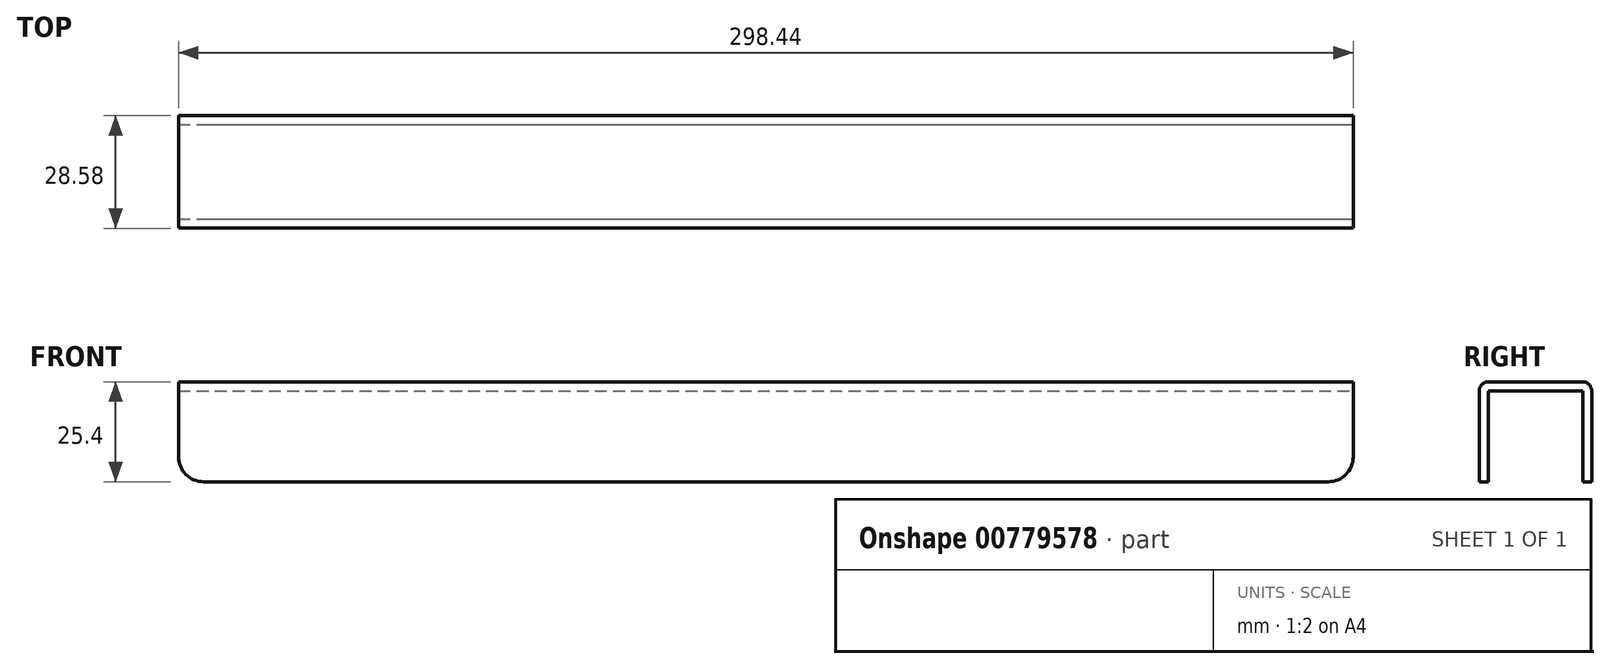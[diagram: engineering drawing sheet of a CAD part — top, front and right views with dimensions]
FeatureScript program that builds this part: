
annotation { "Feature Type Name" : "Feature", "Feature Type Description" : "" }
export const myFeature = defineFeature(function(context is Context, id is Id, definition is map)
    precondition{}
    {
        {
            var Q0;
            Q0=qCreatedBy(makeId("Top.planeOp"),FACE);
            var sketch = newSketch(context, id + "F0", { "sketchPlane" : qUnion([Q0])});
            skLineSegment(sketch, "E0.bottom", {"start": v(-149.23, 14.29) * mm, "end": v(149.23, 14.29) * mm});
            skLineSegment(sketch, "E0.top", {"start": v(-149.23, -14.29) * mm, "end": v(149.23, -14.29) * mm});
            skLineSegment(sketch, "E0.left", {"start": v(-149.23, 14.29) * mm, "end": v(-149.23, -14.29) * mm});
            skLineSegment(sketch, "E0.right", {"start": v(149.23, 14.29) * mm, "end": v(149.23, -14.29) * mm});
            skPoint(sketch, "E0.middle", {"position": v(0, 0) * mm});
            skSolve(sketch);
        }
        {
            var Q0;
            Q0=makeQuery(id+"F0.imprint","IMPRINT",FACE,{"disambiguationData":[TD([[makeQuery(id+"F0.imprint","IMPRINT",EDGE,{"derivedFrom":sQuery(id+"F0.wireOp",EDGE,"E0.bottom")}),-1.0]])]});
            extrude(context, id + "F1", {"entities" : qUnion([Q0]), "depth" : 2.3 * mm, "offsetDistance" : 25.4 * mm});
        }
        {
            var Q0;
            Q0=makeQuery(id+"F1.opExtrude","CAP_FACE",FACE,{"disambiguationData":[OSD([sQuery(id+"F0.wireOp",EDGE,"E0.bottom"),sQuery(id+"F0.wireOp",EDGE,"E0.top"),sQuery(id+"F0.wireOp",EDGE,"E0.left"),sQuery(id+"F0.wireOp",EDGE,"E0.right")])],"isStart":true});
            var sketch = newSketch(context, id + "F2", { "sketchPlane" : qUnion([Q0])});
            skLineSegment(sketch, "E1", {"start": v(-149.23, 14.29) * mm, "end": v(-149.23, 12) * mm});
            skLineSegment(sketch, "E2", {"start": v(-149.23, 12) * mm, "end": v(149.23, 12) * mm});
            skLineSegment(sketch, "E3", {"start": v(-149.23, -14.29) * mm, "end": v(-149.23, -12) * mm});
            skLineSegment(sketch, "E4", {"start": v(-149.23, -12) * mm, "end": v(149.23, -12) * mm});
            skSolve(sketch);
        }
        {
            var Q0;
            Q0=makeQuery(id+"F2.imprint","IMPRINT",FACE,{"disambiguationData":[TD([[makeQuery(id+"F2.imprint","IMPRINT",EDGE,{"derivedFrom":sQuery(id+"F2.wireOp",EDGE,"E1")}),-1.0]])]});
            var Q1;
            Q1=makeQuery(id+"F2.imprint","IMPRINT",FACE,{"disambiguationData":[TD([[makeQuery(id+"F2.imprint","IMPRINT",EDGE,{"derivedFrom":sQuery(id+"F2.wireOp",EDGE,"E3")}),-1.0]])]});
            extrude(context, id + "F3", {"entities" : qUnion([Q0, Q1]), "operationType" : NewBodyOperationType.ADD, "depth" : 23.1 * mm, "offsetDistance" : 25.4 * mm});
        }
        {
            var Q0;
            Q0=makeQuery(id+"F1.opExtrude","CAP_EDGE",EDGE,{"disambiguationData":[OSD([sQuery(id+"F0.wireOp",EDGE,"E0.top")])],"isStart":false});
            var Q1;
            Q1=makeQuery(id+"F1.opExtrude","CAP_EDGE",EDGE,{"disambiguationData":[OSD([sQuery(id+"F0.wireOp",EDGE,"E0.bottom")])],"isStart":false});
            fillet(context, id + "F4", {"entities" : qUnion([Q0, Q1]), "radius" : 2.3 * mm, "tangentPropagation" : true, "allowEdgeOverflow" : false});
        }
        {
            var Q0;
            {var subQ0=sQuery(id+"F0.wireOp",EDGE,"E0.right");var subQ1=makeQuery(id+"F1.opExtrude","CAP_EDGE",EDGE,{"disambiguationData":[OSD([subQ0])],"isStart":true});Q0=makeQuery(id+"F3.opExtrude","CAP_EDGE",EDGE,{"disambiguationData":[OSD([subQ0]),TDD([makeQuery(id+"F2.imprint","IMPRINT",EDGE,{"disambiguationData":[TD([[makeQuery(id+"F2.imprint","INTERSECT",VERTEX,{"derivedFrom":[makeQuery(id+"F1.opExtrude","CAP_EDGE",EDGE,{"disambiguationData":[OSD([sQuery(id+"F0.wireOp",EDGE,"E0.top")])],"isStart":true}),subQ1]}),1.0]])],"derivedFrom":subQ1})])],"isStart":false});}
            fillet(context, id + "F5", {"entities" : qUnion([Q0]), "radius" : 6.35 * mm, "tangentPropagation" : true, "allowEdgeOverflow" : false});
        }
        {
            var Q0;
            {var subQ0=sQuery(id+"F0.wireOp",EDGE,"E0.right");var subQ1=makeQuery(id+"F1.opExtrude","CAP_EDGE",EDGE,{"disambiguationData":[OSD([subQ0])],"isStart":true});Q0=makeQuery(id+"F3.opExtrude","CAP_EDGE",EDGE,{"disambiguationData":[OSD([subQ0]),TDD([makeQuery(id+"F2.imprint","IMPRINT",EDGE,{"disambiguationData":[TD([[makeQuery(id+"F2.imprint","INTERSECT",VERTEX,{"derivedFrom":[makeQuery(id+"F1.opExtrude","CAP_EDGE",EDGE,{"disambiguationData":[OSD([sQuery(id+"F0.wireOp",EDGE,"E0.bottom")])],"isStart":true}),subQ1]}),-1.0]])],"derivedFrom":subQ1})])],"isStart":false});}
            fillet(context, id + "F6", {"entities" : qUnion([Q0]), "radius" : 6.35 * mm, "tangentPropagation" : true, "allowEdgeOverflow" : false});
        }
        {
            var Q0;
            Q0=makeQuery(id+"F3.opExtrude","CAP_EDGE",EDGE,{"disambiguationData":[OSD([sQuery(id+"F2.wireOp",EDGE,"E1")])],"isStart":false});
            var Q1;
            Q1=makeQuery(id+"F3.opExtrude","CAP_EDGE",EDGE,{"disambiguationData":[OSD([sQuery(id+"F2.wireOp",EDGE,"E3")])],"isStart":false});
            fillet(context, id + "F7", {"entities" : qUnion([Q0, Q1]), "radius" : 6.35 * mm, "tangentPropagation" : true, "allowEdgeOverflow" : false});
        }
    });
